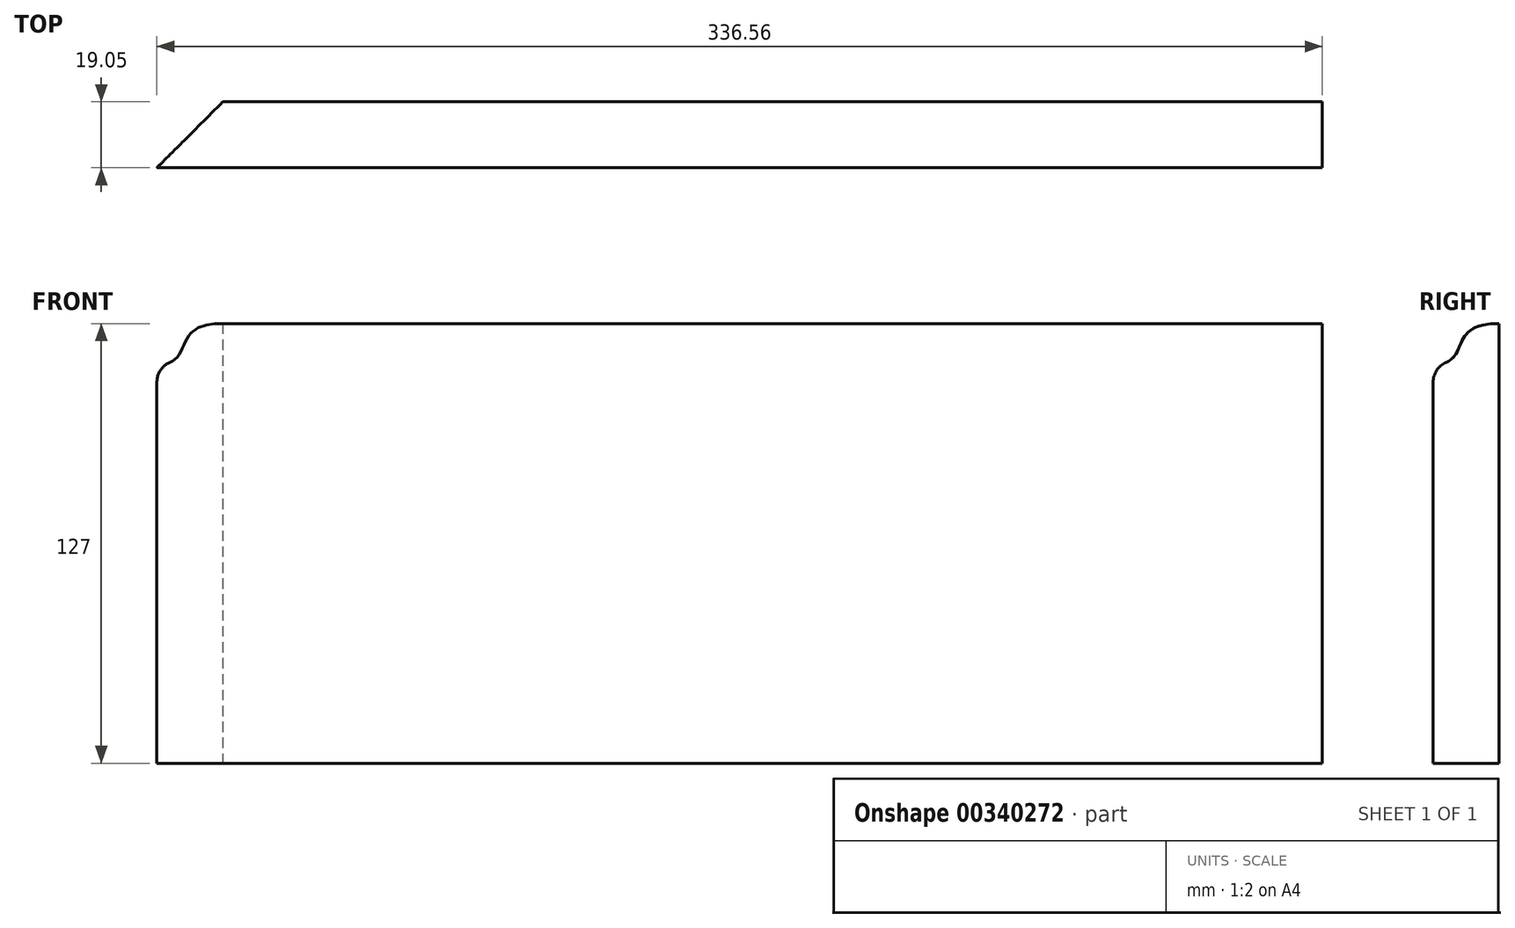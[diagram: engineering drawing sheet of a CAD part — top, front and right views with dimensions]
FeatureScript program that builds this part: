
annotation { "Feature Type Name" : "Feature", "Feature Type Description" : "" }
export const myFeature = defineFeature(function(context is Context, id is Id, definition is map)
    precondition{}
    {
        {
            var Q0;
            Q0=qCreatedBy(makeId("Front.planeOp"),FACE);
            var sketch = newSketch(context, id + "F0", { "sketchPlane" : qUnion([Q0])});
            skLineSegment(sketch, "E0.bottom", {"start": v(168.28, -63.5) * mm, "end": v(-168.28, -63.5) * mm});
            skLineSegment(sketch, "E0.top", {"start": v(168.28, 63.5) * mm, "end": v(-168.28, 63.5) * mm});
            skLineSegment(sketch, "E0.left", {"start": v(168.28, -63.5) * mm, "end": v(168.28, 63.5) * mm});
            skLineSegment(sketch, "E0.right", {"start": v(-168.28, -63.5) * mm, "end": v(-168.28, 63.5) * mm});
            skPoint(sketch, "E0.middle", {"position": v(0, 0) * mm});
            skSolve(sketch);
        }
        {
            var Q0;
            Q0=qSketchRegion(id+"F0",true);
            extrude(context, id + "F1", {"entities" : qUnion([Q0]), "depth" : 19.05 * mm});
        }
        {
            var Q0;
            Q0=makeQuery(id+"F1.opExtrude","SWEPT_FACE",FACE,{"disambiguationData":[OSD([sQuery(id+"F0.wireOp",EDGE,"E0.left")])]});
            var sketch = newSketch(context, id + "F2", { "sketchPlane" : qUnion([Q0])});
            skFitSpline(sketch, "E1", {"points": [v(0, 63.5) * mm, v(-19.05, 51.53) * mm], "startDerivative": vector(-48.08, 0) * mm, "endDerivative": vector(-35.63, -1.9) * mm});
            skArc(sketch, "E2.filletArc", {"start": v(-15.26, 52.32) * mm, "mid": v(-18.02, 49.98) * mm, "end": v(-19.05, 46.5) * mm});
            skLineSegment(sketch, "E3", {"start": v(0, 63.5) * mm, "end": v(-19.05, 63.5) * mm});
            skLineSegment(sketch, "E4", {"start": v(-19.05, 63.5) * mm, "end": v(-19.05, 46.5) * mm});
            skSolve(sketch);
        }
        {
            var Q0;
            Q0=qSketchRegion(id+"F2",true);
            extrude(context, id + "F3", {"entities" : qUnion([Q0]), "operationType" : NewBodyOperationType.REMOVE, "endBound" : BoundingType.THROUGH_ALL, "oppositeDirection" : true, "depth" : 25.4 * mm});
        }
        {
            var Q0;
            Q0=makeQuery(id+"F1.opExtrude","SWEPT_FACE",FACE,{"disambiguationData":[OSD([sQuery(id+"F0.wireOp",EDGE,"E0.bottom")])]});
            var sketch = newSketch(context, id + "F4", { "sketchPlane" : qUnion([Q0])});
            skLineSegment(sketch, "E5", {"start": v(-168.28, 19.05) * mm, "end": v(-168.28, 0) * mm});
            skLineSegment(sketch, "E6", {"start": v(0, 19.05) * mm, "end": v(0, 0) * mm, "construction": true});
            skLineSegment(sketch, "E7", {"start": v(-168.28, 0) * mm, "end": v(-149.22, 0) * mm});
            skLineSegment(sketch, "E8", {"start": v(-149.22, 0) * mm, "end": v(-168.28, 19.05) * mm});
            skSolve(sketch);
        }
        {
            var Q0;
            Q0=qSketchRegion(id+"F4",true);
            extrude(context, id + "F5", {"entities" : qUnion([Q0]), "operationType" : NewBodyOperationType.REMOVE, "endBound" : BoundingType.THROUGH_ALL, "oppositeDirection" : true, "depth" : 25.4 * mm});
        }
    });
